# Revit family: Artemide_Tagora_Recessed_570
name_source: partatom
category: Apparecchi per illuminazione
revit_build: Autodesk Revit 2018 (Build: 20190510_1515(x64)
units: mm (PartAtom-declared; Revit-internal decimal feet)

## family parameters
Basato su piano di lavoro = Sì
Condiviso = No
Punto di calcolo locali = No
Quota connettore circolare = Usa diametro
Sempre verticale = Sì
Sorgente d'illuminazione = Sì
Taglio con vuoti quando caricato = Sì
Tipo di parte = Normale

## types (1)
- Artemide_Tagora_Recessed_570
    6 Monthly = -
    Access Clearance Bottom = 0
    Access Clearance Front = 0
    Access Clearance Left = 0
    Access Clearance Rear = 0
    Access Clearance Right = 0
    Access Clearance Top = 0
    Air Handling = -
    Ambient Temperature                             = 0
    Angolo inclinazione = 90.00°
    Annually = -
    Application Environment = Internal
    Basis of lifetime lumen depreciation   = 0
    Basis of lifetime luminaire failures        = 0
    Beam Angle Longditudinal Axis  = 0.00°
    Beam Angle Transverse Axis  = 0.00°
    Bespoke Timeframe = -
    CE Approval = Y
    Colour Rendering Index = 80
    Colour Temperature = 4000
    Column = -
    Control Gear Location = -
    Control Gear Required = -
    Control Gear Standby Power  = 0
    Control Gear Type = -
    Current  = 0
    Cut Out Length = 186
    Cut Out Width = 606
    Daily = -
    Daylight Sensor = -
    Diffusing screen = -
    Downward Component = 0
    Drive Current                                          = 0
    Duration of Integral Emergency Lighting  = 0
    ENEC Certification of European conformity = N
    Earth Point  = -
    Efficiency = 43
    Embodied Carbon  = 0
    Emergency = N
    Emergency Charging Power       = 0
    Emergency Lighting Battery = -
    Emergency light output percentage = 0
    Emetti da diametro cerchio = 475 mm  [stored 1.5584 ft]
    End Caps/Transition Caps/Joints = -
    Environmental Product Declaration = -
    Expected Life = -
    External Control Line Voltage = 0
    Face Length = 0
    Face Shape = Circular
    Face Width = 0
    Features = Any additional components/accessories included in this file are required to complete the product/configuration and must be ordered separately.Please check the catalogue/dedicated brochure for more information
    File diagramma fotometrico = M250321.IES
    Filtro dei colori = 16777215
    Fire Rated = -
    Fire Rated Temperature = 0
    Fire Rating Duration = 0
    Fire Shroud = -
    Fixings = -
    Frequency  = 0
    Green Guide for Specification = -
    Gross Weight = 0
    Hazardous Area Category = -
    Hazardous Area Protection Type = -
    Housing Colour  = White
    Housing Finish  = Painted
    Housing Material = Aluminium
    IES Files  = https://www.artemide.com
    IK Rating = -
    IP Rating = IP20
    IfcExportAs = IfcLightFixtureType
    IfcExportType = NOT DEFINED
    Infills = -
    Initial Lumens = 3820
    Input Lumens Direct light = 8880
    Input Lumens Indirect light = 0
    Integral Emergency Lighting Battery Type = -
    Integral Fuse or Circuit Protection  = -
    Intended Market = Unset
    International Type Code = -
    LED Initial Colour Variation                      = 0
    LED Maintained Colour Variation         = 0
    LED lifetime = 50000
    Lamp Cap = LED Integrated
    Lamp Included = Y
    Lamp Replacement Interval = -
    Lamp Survival Factor = -
    Life Cycle Analysis = -
    Light Fixture Mounting Type = Recessed
    Light Output Pattern = -
    Location of Manufacturer = -
    Louvre/Lens = -
    Luminaire Cleaning Interval  = -
    Luminaire Maintenance Factor = 0
    Luminaire Type = Downlight
    Luminance at 65deg Angle = 0
    M_Diffuser = Artemide_Glass_LightBulb
    M_Fixings = Artemide_Aluminum_Anodized
    M_Housing = Artemide_Aluminum_White
    Maintenance Required: 0-300hrs  = -
    Maintenance Required: 1001-2000hrs  = -
    Maintenance Required: 2001-4000hrs  = -
    Maintenance Required: 301-600hrs  = -
    Maintenance Required: 4001-8000hrs  = -
    Maintenance Required: 601-1000hrs = -
    Maintenance Required: 8001-12000hrs  = -
    Manufacturer Website = https://www.artemide.com
    Material Ingredient Reporting = -
    Max Height from ceiling = 0 mm  [stored 0 ft]
    Maximum Operating Temperature = 0
    Minimum Operating Temperature = 0
    Monthly = -
    Motion Detector = -
    Motion Sensor = -
    Number of Poles = 0
    Number of Primary Lamps = 1
    Number of Secondary Lamps = 0
    Output Lumens Direct light = 3820
    Output Lumens Indirect light = 0
    Overall Height = 0
    Overall Length = 642
    Overall Light Output Ratio = 0
    Overall Width = 0
    Photocell = -
    Power Factor = 0
    Power Supply Kit = -
    Primary Lamp Type = LED
    Product Literature = https://www.artemide.com
    Product Model Number = M250321
    Product Range = Tagora
    Produttore = Artemide
    Prospetto di default = 1219 mm
    Quarterly = -
    Rated Lamp Life = 50000
    Rendi la forma visibile nel rendering = No
    Responsible Extraction of Materials = -
    Responsible Sourcing of Materials = -
    Secondary Lamp = -
    Secondary Lamp Cap = -
    Secondary Lamp Colour Rendering Index = 0
    Secondary Lamp Colour Temperature = 0
    Secondary Lamp Efficacy = 0
    Secondary Lamp Included = -
    Secondary Lamp Initial Lumens  = 0
    Secondary Lamp International Type Code = -
    Secondary Lamp Voltage = 0
    Secondary Rated Lamp Life = 0
    Service life  = -
    Shipping Weight = 0
    Standards = -
    Suitable Dimmer Type = DALI
    Suitable for Dimming  = Y
    Suitable for Motion Detector Control = N
    Suitable for Photocell Control = -
    Supply Phase = 0
    Testing method = -
    Total Light Output  = 0
    Total Power = 0
    Trim Colour  = White
    Trim Finish = Painted
    Trim Material = Aluminium
    URL to Energy Technology List = -
    URL to O&M Manual = https://www.artemide.com
    Uniclass 2015 = Pr_70_70_48
    Unified Glare Rating  = -
    Upward Component  = 0
    Variazione temperatura colore lampada con luminosità attenuata = <Nessuno>
    Voltage = -
    Warranty ID = https://cloud.artemide.com
    Weekly = -

note: [stored X ft] marks values corroborated as IEEE doubles in the binary element streams (Revit-internal decimal feet)

## geometry (parser evidence)
native form markers: Sweep x1
no freeform markers — native parametric forms only
